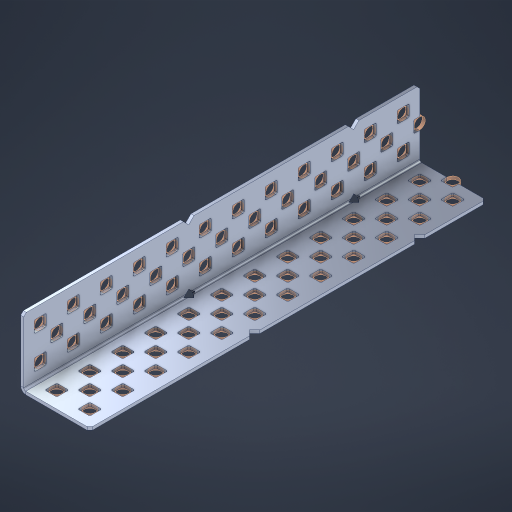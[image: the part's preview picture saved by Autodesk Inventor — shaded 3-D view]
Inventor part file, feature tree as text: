
AUTODESK INVENTOR PART (.ipt)
format: ipt  version: 2023 (Build 270158000, 158)  size: 1,092,096 bytes
history: native  units: in
note: dims shown in document units (in); Inventor stores cm internally (conversion verified against a paired STEP export)
features: other x78, extrude x70, sheet_metal_op x8, sketch x7, pattern_linear x2, mirror x1, chamfer x1
ambient origin geometry x8: Origin, YZ Plane, XZ Plane, XY Plane, X Axis, Y Axis, Z Axis, Center Point
bodies: Solid1 (feature_tree), Body (feature_tree)
feature tree (167):
  sheet_metal_op  "Flanges"
  sheet_metal_op  "Body Pattern"
  pattern_linear  "Center Pattern"  Spacing1=1.0in  [1 undecoded]
  other  "Arc Length"
  pattern_linear  "Notch Pattern"  Spacing1=0.1875in  [1 undecoded]
  other  "Diagonal Plane"
  mirror  "Everything Mirrored"
  chamfer  "End Chamfer"
  sketch  "Sketch1"  dims[d0=1.0in]
  other  "Plate1"
  sketch  "Sketch2"  dims[d1=6.0in]
  other  "Plate2"
  sheet_metal_op  "Bend1"
  sheet_metal_op  "Corner1"
  sketch  "Sketch8"  dims[d2=0.0469in]
  sketch  "Sketch9"  dims[d3=0.0469in]
  other  "Srf91"
  sheet_metal_op  "Body Pattern Sketch"
  other  "Srf92"
  sketch  "Sketch13"  dims[d4=0.0234in]
  sketch  "Sketch15"  dims[d5=0.0938in]
  sketch  "Sketch16"  dims[d6=0.0469in d7=1.0in d8=90.0deg d9=0.0312in d10=0.1875in d11=0.0469in d12=0.0469in d49=0.182in d50=0.02in d52=0.25in d53=0.0469in d54=0.0in d55=0.172in d56=1.0in d57=0.0in d60=4.7244in d62=0.5in d63=0.7874in d65=0.5in d85=0.1473in d86=0.1659in d89=0.0469in d90=0.0in d91=0.04in d92=0.0491in d95=2.5in d96=0.04in d97=0.25in d98=45.0deg d99=0.25in d106=0.182in d107=0.02in d108=0.5in d110=0.0469in d111=0.0in d112=0.172in d113=0.5in d114=0.0in d117=0.5in d123=0.25in d125=0.25in d126=0.0491in d127=0.1227in d128=0.08in d129=0.04in d130=2.5in]
  other  "Srf786"
  other  "Srf856"
  other  "Srf857"
  other  "Srf858"
  other  "Srf859"
  other  "Srf860"
  other  "Srf861"
  other  "Srf889"
  other  "Srf890"
  other  "Srf891"
  other  "Srf1275"
  other  "Srf1276"
  other  "Srf1278"
  other  "Srf1279"
  other  "Srf1280"
  other  "Srf1281"
  other  "Srf1282"
  other  "Srf1283"
  other  "Srf1277"
  other  "Srf1285"
  other  "Srf1286"
  other  "Srf1287"
  other  "Srf1383"
  other  "Srf1384"
  other  "Srf1385"
  other  "Srf1386"
  other  "Srf1387"
  other  "Srf1388"
  other  "Srf1389"
  other  "Srf1390"
  other  "Srf1391"
  other  "Srf1392"
  other  "Srf1393"
  other  "Srf1394"
  other  "Srf1395"
  other  "Srf1396"
  other  "Srf1397"
  other  "Srf1398"
  other  "Srf1445"
  other  "Srf1446"
  other  "Srf1447"
  other  "Srf1448"
  other  "Srf1449"
  other  "Srf1450"
  other  "Srf1451"
  other  "Srf1452"
  other  "Srf1475"
  other  "Srf1476"
  other  "Srf1477"
  other  "Srf1478"
  other  "Srf1479"
  other  "Srf1480"
  other  "Srf1481"
  other  "Srf1482"
  other  "Srf1483"
  other  "Srf1484"
  other  "Srf1485"
  other  "Srf1486"
  other  "Srf1487"
  other  "Srf1488"
  other  "Srf1489"
  other  "Srf1490"
  other  "Srf1537"
  other  "Srf1538"
  other  "Srf1539"
  other  "Srf1540"
  other  "Srf1541"
  other  "Srf1542"
  other  "Srf1543"
  other  "Srf1544"
  sheet_metal_op  "Body Stamp"
  sheet_metal_op  "Body Circle"
  other  "Center Stamp"
  other  "Center Circle"
  sheet_metal_op  "Notch"
  extrude  "ExtrusionSrf92"  Depth=0.0469in
  extrude  "ExtrusionSrf856"  Depth=0.0469in
  extrude  "ExtrusionSrf857"  Depth=0.182in
  extrude  "ExtrusionSrf858"  Depth=0.02in
  extrude  "ExtrusionSrf859"  Depth=0.25in
  extrude  "ExtrusionSrf860"  Depth=0.0469in
  extrude  "ExtrusionSrf861"  TaperAngle=0.0deg  [1 undecoded]
  extrude  "ExtrusionSrf889"  Depth=2.5in
  extrude  "ExtrusionSrf890"  Depth=1.0in TaperAngle=0.0deg
  extrude  "ExtrusionSrf891"  Depth=2.5in
  extrude  "ExtrusionSrf1275"  Depth=0.5in
  extrude  "ExtrusionSrf1276"  Depth=2.5in
  extrude  "ExtrusionSrf1277"  Depth=2.5in
  extrude  "ExtrusionSrf1278"  Depth=0.0469in
  extrude  "ExtrusionSrf1279"  Depth=2.5in TaperAngle=0.0deg
  extrude  "ExtrusionSrf1280"  Depth=2.5in
  extrude  "ExtrusionSrf1281"  Depth=0.25in TaperAngle=45.0deg
  extrude  "ExtrusionSrf1282"  Depth=0.25in
  extrude  "ExtrusionSrf1345"  Depth=0.182in
  extrude  "ExtrusionSrf1346"  Depth=0.02in
  extrude  "ExtrusionSrf1347"  Depth=0.5in
  extrude  "ExtrusionSrf1348"  Depth=0.0469in
  extrude  "ExtrusionSrf1383"  TaperAngle=0.0deg  [1 undecoded]
  extrude  "ExtrusionSrf1384"  Depth=2.5in
  extrude  "ExtrusionSrf1385"  Depth=0.5in TaperAngle=0.0deg
  extrude  "ExtrusionSrf1386"  Depth=0.5in
  extrude  "ExtrusionSrf1387"  Depth=0.25in
  extrude  "ExtrusionSrf1388"  Depth=0.25in
  extrude  "ExtrusionSrf1389"  Depth=2.5in
  extrude  "ExtrusionSrf1390"  Depth=2.5in
  extrude  "ExtrusionSrf1391"  Depth=2.5in
  extrude  "ExtrusionSrf1392"  Depth=2.5in
  extrude  "ExtrusionSrf1393"  Depth=2.5in
  extrude  "ExtrusionSrf1394"  [1 undecoded]
  extrude  "ExtrusionSrf1395"  [1 undecoded]
  extrude  "ExtrusionSrf1396"  [1 undecoded]
  extrude  "ExtrusionSrf1397"  [1 undecoded]
  extrude  "ExtrusionSrf1398"  [1 undecoded]
  extrude  "ExtrusionSrf1445"  [1 undecoded]
  extrude  "ExtrusionSrf1446"  [1 undecoded]
  extrude  "ExtrusionSrf1447"  [1 undecoded]
  extrude  "ExtrusionSrf1448"  [1 undecoded]
  extrude  "ExtrusionSrf1449"  [1 undecoded]
  extrude  "ExtrusionSrf1450"  [1 undecoded]
  extrude  "ExtrusionSrf1451"  [1 undecoded]
  extrude  "ExtrusionSrf1452"  [1 undecoded]
  extrude  "ExtrusionSrf1475"  [1 undecoded]
  extrude  "ExtrusionSrf1476"  [1 undecoded]
  extrude  "ExtrusionSrf1477"  [1 undecoded]
  extrude  "ExtrusionSrf1478"  [1 undecoded]
  extrude  "ExtrusionSrf1479"  [1 undecoded]
  extrude  "ExtrusionSrf1480"  [1 undecoded]
  extrude  "ExtrusionSrf1481"  [1 undecoded]
  extrude  "ExtrusionSrf1482"  [1 undecoded]
  extrude  "ExtrusionSrf1483"  [1 undecoded]
  extrude  "ExtrusionSrf1484"  [1 undecoded]
  extrude  "ExtrusionSrf1485"  [1 undecoded]
  extrude  "ExtrusionSrf1486"  [1 undecoded]
  extrude  "ExtrusionSrf1487"  [1 undecoded]
  extrude  "ExtrusionSrf1488"  [1 undecoded]
  extrude  "ExtrusionSrf1489"  [1 undecoded]
  extrude  "ExtrusionSrf1490"  [1 undecoded]
  extrude  "ExtrusionSrf1537"  [1 undecoded]
  extrude  "ExtrusionSrf1538"  [1 undecoded]
  extrude  "ExtrusionSrf1539"  [1 undecoded]
  extrude  "ExtrusionSrf1540"  [1 undecoded]
  extrude  "ExtrusionSrf1541"  [1 undecoded]
  extrude  "ExtrusionSrf1542"  [1 undecoded]
  extrude  "ExtrusionSrf1543"  [1 undecoded]
  extrude  "ExtrusionSrf1544"  [1 undecoded]
note: 41 required parameter values undecoded (feature->parameter linkage not recoverable at this tier; creation-order binding heuristic only, values carry confidence <= 0.55)
